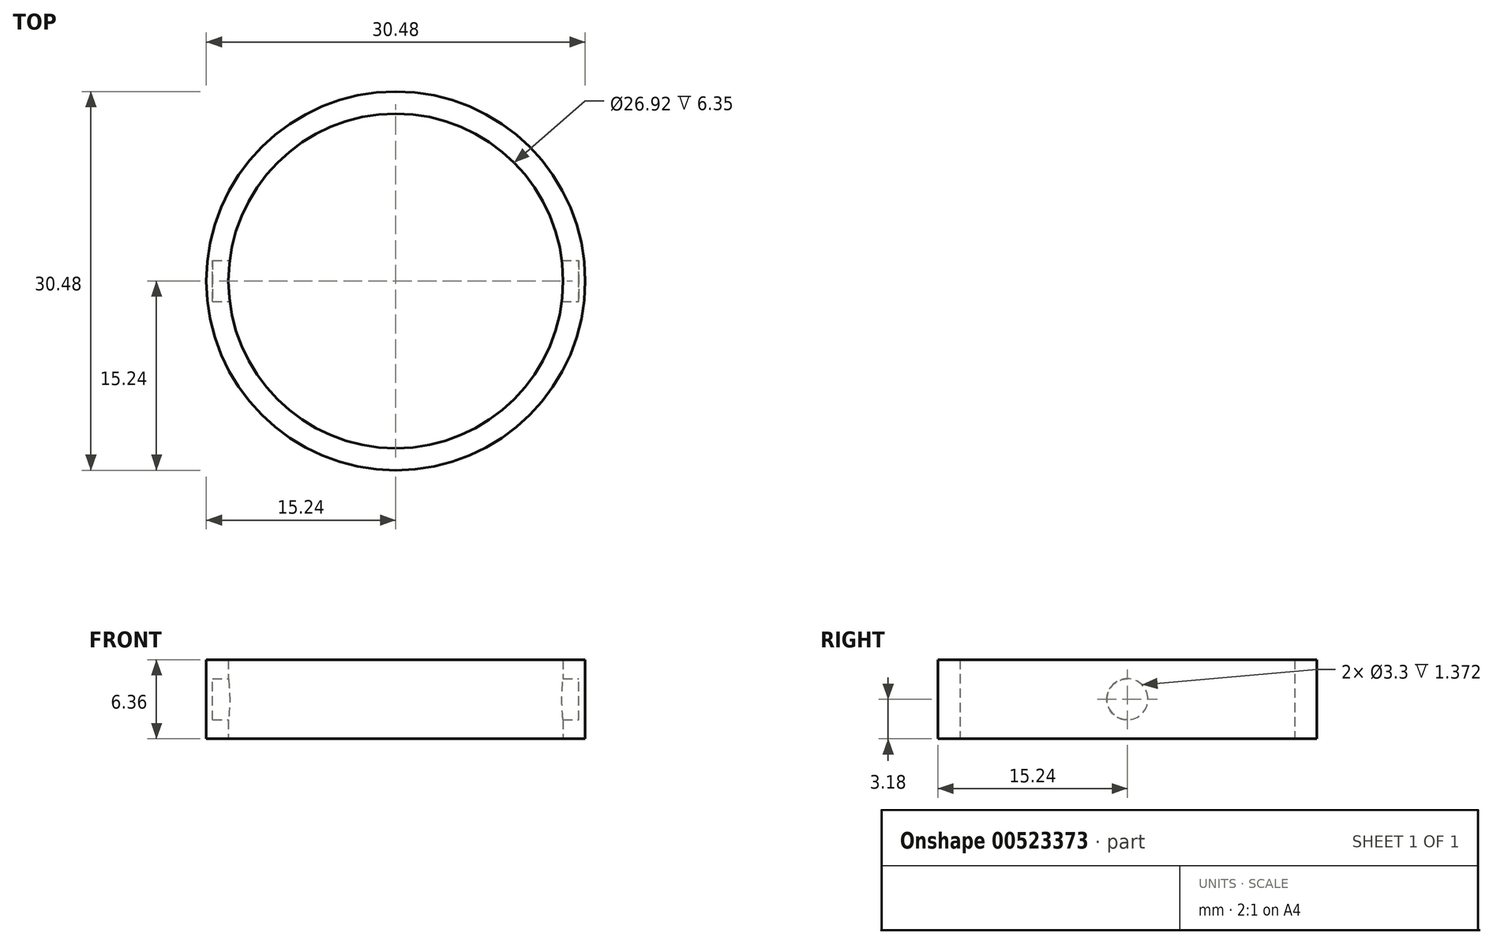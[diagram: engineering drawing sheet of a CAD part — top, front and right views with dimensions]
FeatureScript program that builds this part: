
annotation { "Feature Type Name" : "Feature", "Feature Type Description" : "" }
export const myFeature = defineFeature(function(context is Context, id is Id, definition is map)
    precondition{}
    {
        {
            var Q0;
            Q0=qCreatedBy(makeId("Top.planeOp"),FACE);
            var sketch = newSketch(context, id + "F0", { "sketchPlane" : qUnion([Q0])});
            skCircle(sketch, "E0", {"center": v(0, 0) * mm, "radius": 15.24 * mm});
            skCircle(sketch, "E1", {"center": v(0, 0) * mm, "radius": 13.46 * mm});
            skSolve(sketch);
        }
        {
            var Q0;
            Q0=makeQuery(id+"F0.imprint","IMPRINT",FACE,{"disambiguationData":[TD([[makeQuery(id+"F0.imprint","IMPRINT",EDGE,{"derivedFrom":sQuery(id+"F0.wireOp",EDGE,"E0")}),1.0]])]});
            extrude(context, id + "F1", {"entities" : qUnion([Q0]), "endBound" : BoundingType.SYMMETRIC, "depth" : 6.35 * mm, "offsetDistance" : 25.4 * mm});
        }
        {
            var Q0;
            Q0=qCreatedBy(makeId("Right.planeOp"),FACE);
            var sketch = newSketch(context, id + "F2", { "sketchPlane" : qUnion([Q0])});
            skCircle(sketch, "E2", {"center": v(0, 0) * mm, "radius": 1.65 * mm});
            skSolve(sketch);
        }
        {
            var Q0;
            Q0=makeQuery(id+"F2.imprint","IMPRINT",FACE,{"disambiguationData":[TD([[makeQuery(id+"F2.imprint","IMPRINT",EDGE,{"derivedFrom":sQuery(id+"F2.wireOp",EDGE,"E2")}),1.0]])]});
            extrude(context, id + "F3", {"entities" : qUnion([Q0]), "operationType" : NewBodyOperationType.REMOVE, "oppositeDirection" : true, "depth" : 14.73 * mm, "offsetDistance" : 25.4 * mm, "hasSecondDirection" : true, "secondDirectionOppositeDirection" : false, "secondDirectionDepth" : 14.73 * mm});
        }
    });
